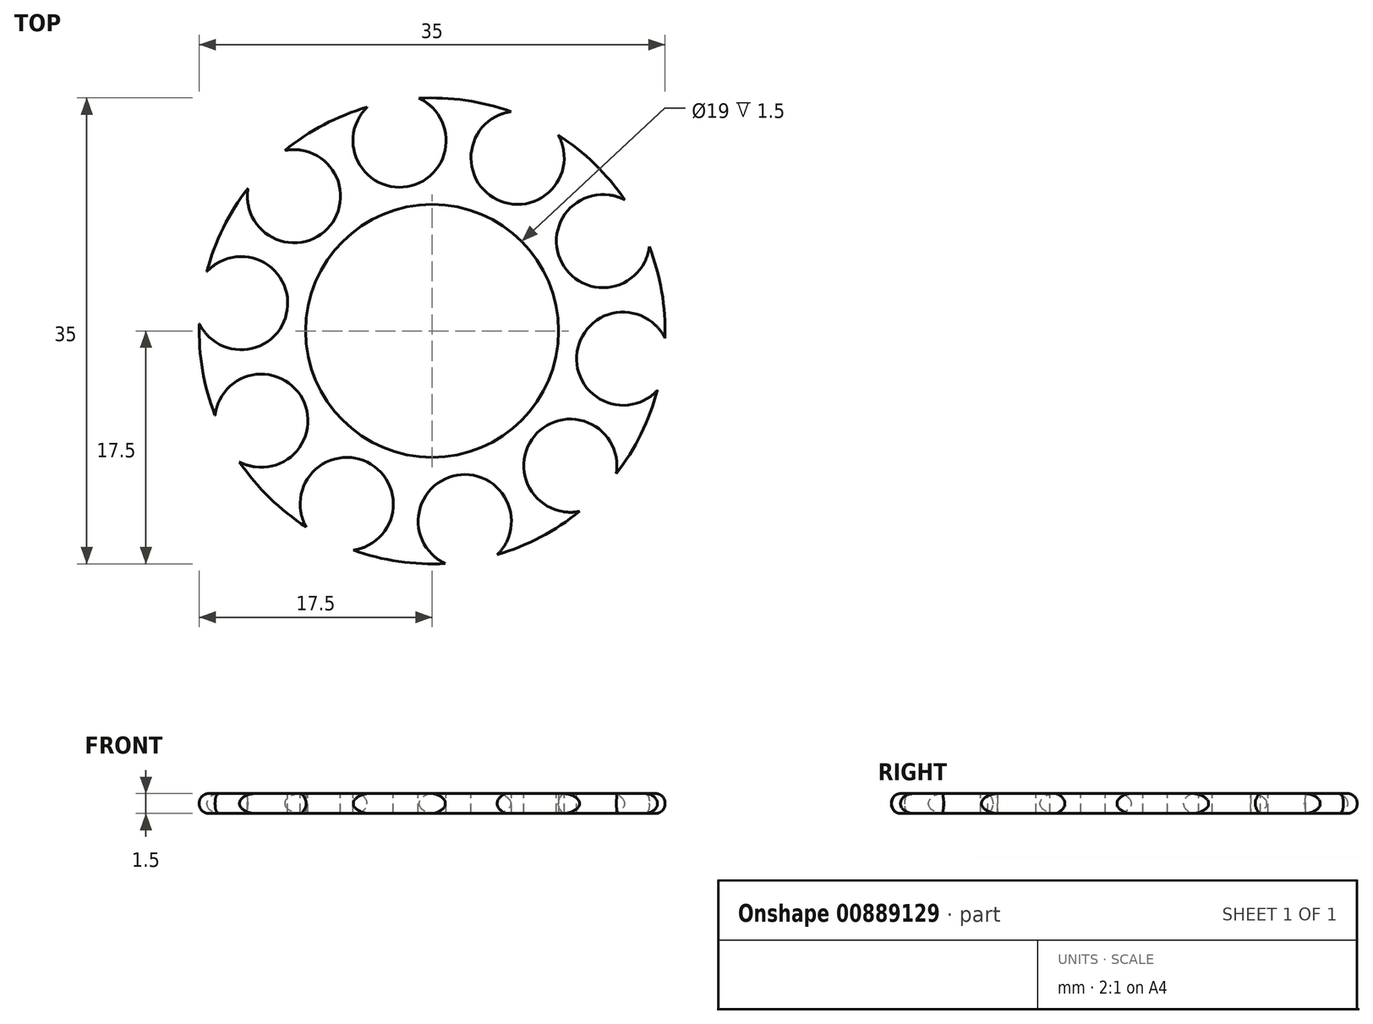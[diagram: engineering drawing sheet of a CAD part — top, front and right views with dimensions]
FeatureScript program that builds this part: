
annotation { "Feature Type Name" : "Feature", "Feature Type Description" : "" }
export const myFeature = defineFeature(function(context is Context, id is Id, definition is map)
    precondition{}
    {
        {
            var Q0;
            Q0=qCreatedBy(makeId("Top.planeOp"),FACE);
            var sketch = newSketch(context, id + "F0", { "sketchPlane" : qUnion([Q0])});
            skCircle(sketch, "E0", {"center": v(0, 0) * mm, "radius": 9.5 * mm});
            skCircle(sketch, "E1", {"center": v(0, 0) * mm, "radius": 17.5 * mm});
            skSolve(sketch);
        }
        {
            var Q0;
            Q0 = qSketchRegion(id + "F0", true);
            extrude(context, id + "F1", {"entities" : qUnion([Q0]), "depth" : 1.5 * mm, "offsetDistance" : 25 * mm});
        }
        {
            var Q0;
            Q0=makeQuery(id+"F1.opExtrude","CAP_FACE",FACE,{"disambiguationData":[OSD([sQuery(id+"F0.wireOp",EDGE,"E0"),sQuery(id+"F0.wireOp",EDGE,"E1")])],"isStart":false});
            var sketch = newSketch(context, id + "F2", { "sketchPlane" : qUnion([Q0])});
            skCircle(sketch, "E2", {"center": v(-10.38, 10.12) * mm, "radius": 3.5 * mm});
            skCircle(sketch, "E3.1.0", {"center": v(-14.35, 2.09) * mm, "radius": 3.5 * mm});
            skCircle(sketch, "E3.2.0", {"center": v(-12.83, -6.75) * mm, "radius": 3.5 * mm});
            skCircle(sketch, "E3.3.0", {"center": v(-6.42, -13) * mm, "radius": 3.5 * mm});
            skCircle(sketch, "E3.4.0", {"center": v(2.45, -14.3) * mm, "radius": 3.5 * mm});
            skCircle(sketch, "E3.5.0", {"center": v(10.38, -10.12) * mm, "radius": 3.5 * mm});
            skCircle(sketch, "E3.6.0", {"center": v(14.35, -2.09) * mm, "radius": 3.5 * mm});
            skCircle(sketch, "E3.7.0", {"center": v(12.83, 6.75) * mm, "radius": 3.5 * mm});
            skCircle(sketch, "E3.8.0", {"center": v(6.42, 13) * mm, "radius": 3.5 * mm});
            skCircle(sketch, "E3.9.0", {"center": v(-2.45, 14.3) * mm, "radius": 3.5 * mm});
            skPoint(sketch, "E3.center", {"position": v(0, 0) * mm});
            skSolve(sketch);
        }
        {
            var Q0;
            Q0 = qSketchRegion(id + "F2", true);
            extrude(context, id + "F3", {"entities" : qUnion([Q0]), "operationType" : NewBodyOperationType.REMOVE, "oppositeDirection" : true, "depth" : 25 * mm, "offsetDistance" : 25 * mm});
        }
        {
            var Q0;
            Q0=makeQuery(id+"F1.opExtrude","CAP_EDGE",EDGE,{"disambiguationData":[OSD([sQuery(id+"F0.wireOp",EDGE,"E1")])],"isStart":false});
            var Q1;
            Q1=makeQuery(id+"F1.opExtrude","CAP_EDGE",EDGE,{"disambiguationData":[OSD([sQuery(id+"F0.wireOp",EDGE,"E1")])],"isStart":true});
            fillet(context, id + "F4", {"entities" : qUnion([Q0, Q1]), "radius" : 0.72 * mm, "tangentPropagation" : true, "allowEdgeOverflow" : false});
        }
    });
